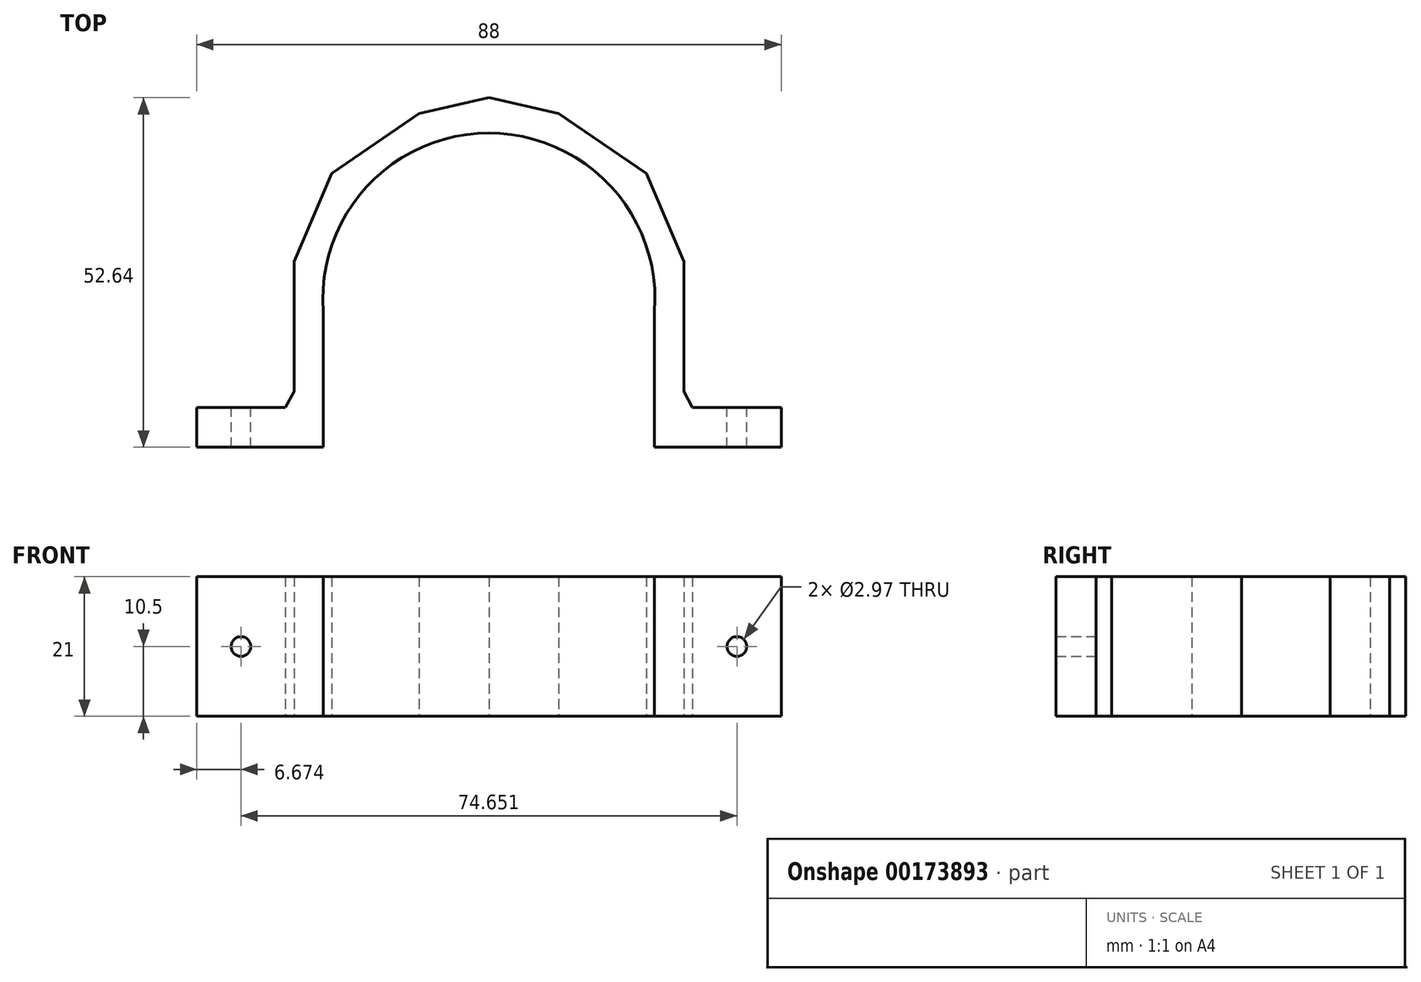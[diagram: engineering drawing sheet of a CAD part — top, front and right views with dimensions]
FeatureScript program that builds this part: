
annotation { "Feature Type Name" : "Feature", "Feature Type Description" : "" }
export const myFeature = defineFeature(function(context is Context, id is Id, definition is map)
    precondition{}
    {
        {
            var Q0;
            Q0=qCreatedBy(makeId("Top.planeOp"),FACE);
            var sketch = newSketch(context, id + "F0", { "sketchPlane" : qUnion([Q0])});
            skArc(sketch, "E0", {"start": v(24.93, 20.42) * mm, "mid": v(0, 47.3) * mm, "end": v(-24.93, 20.42) * mm});
            skLineSegment(sketch, "E1.bottom", {"start": v(28, 22.3) * mm, "end": v(-28, 22.3) * mm});
            skLineSegment(sketch, "E1.top", {"start": v(28, -22.3) * mm, "end": v(-28, -22.3) * mm});
            skPoint(sketch, "E1.middle", {"position": v(0, 0) * mm});
            skLineSegment(sketch, "E2", {"start": v(28, 0) * mm, "end": v(44, 0) * mm});
            skPoint(sketch, "E2.endSnap0", {"position": v(28, 0) * mm});
            skLineSegment(sketch, "E3", {"start": v(44, 0) * mm, "end": v(44, 6) * mm});
            skLineSegment(sketch, "E4", {"start": v(44, 6) * mm, "end": v(30.65, 6) * mm});
            skLineSegment(sketch, "E5", {"start": v(0, 54.2) * mm, "end": v(0, -14.37) * mm, "construction": true});
            skLineSegment(sketch, "E6.MirrorCS", {"start": v(-44, 6) * mm, "end": v(-30.65, 6) * mm});
            skLineSegment(sketch, "E7.MirrorCS", {"start": v(-44, 0) * mm, "end": v(-44, 6) * mm});
            skLineSegment(sketch, "E8.MirrorCS", {"start": v(-28, 0) * mm, "end": v(-44, 0) * mm});
            skLineSegment(sketch, "E9", {"start": v(-29.33, 8.4) * mm, "end": v(-30.65, 6) * mm});
            skLineSegment(sketch, "E10", {"start": v(-30.65, 6) * mm, "end": v(-29.33, 8.4) * mm});
            skLineSegment(sketch, "E11", {"start": v(-29.33, 8.4) * mm, "end": v(-29.33, 27.94) * mm});
            skLineSegment(sketch, "E12", {"start": v(-29.33, 27.94) * mm, "end": v(-23.7, 41.25) * mm});
            skLineSegment(sketch, "E13", {"start": v(-23.7, 41.25) * mm, "end": v(-10.51, 50.24) * mm});
            skLineSegment(sketch, "E14", {"start": v(-10.51, 50.24) * mm, "end": v(0, 52.64) * mm});
            skLineSegment(sketch, "E15.MirrorCS", {"start": v(10.51, 50.24) * mm, "end": v(0, 52.64) * mm});
            skLineSegment(sketch, "E16.MirrorCS", {"start": v(23.7, 41.25) * mm, "end": v(10.51, 50.24) * mm});
            skLineSegment(sketch, "E17.MirrorCS", {"start": v(29.33, 27.94) * mm, "end": v(23.7, 41.25) * mm});
            skLineSegment(sketch, "E18.MirrorCS", {"start": v(29.33, 8.4) * mm, "end": v(29.33, 27.94) * mm});
            skLineSegment(sketch, "E19.MirrorCS", {"start": v(30.65, 6) * mm, "end": v(29.33, 8.4) * mm});
            skPoint(sketch, "E20.orphan", {"position": v(-28, 6) * mm});
            skPoint(sketch, "E21.orphan", {"position": v(-28, 10.8) * mm});
            skPoint(sketch, "E22.orphan", {"position": v(28, 6) * mm});
            skLineSegment(sketch, "E23", {"start": v(-44, 0) * mm, "end": v(44, 0) * mm});
            skLineSegment(sketch, "E24", {"start": v(-24.93, 20.42) * mm, "end": v(-24.93, 0) * mm});
            skLineSegment(sketch, "E25.MirrorCS", {"start": v(24.93, 20.42) * mm, "end": v(24.93, 0) * mm});
            skSolve(sketch);
        }
        {
            var Q0;
            {var subQ7=sQuery(id+"F0.wireOp",EDGE,"E3");Q0=makeQuery(id+"F0.imprint","IMPRINT",FACE,{"disambiguationData":[TD([[makeQuery(id+"F0.imprint","IMPRINT",EDGE,{"derivedFrom":subQ7}),1.0]])]});}
            extrude(context, id + "F1", {"entities" : qUnion([Q0]), "depth" : 21 * mm});
        }
        {
            var Q0;
            Q0=makeQuery(id+"F1.opExtrude","SWEPT_FACE",FACE,{"disambiguationData":[OSD([sQuery(id+"F0.wireOp",EDGE,"E4")])]});
            var sketch = newSketch(context, id + "F2", { "sketchPlane" : qUnion([Q0])});
            skCircle(sketch, "E26", {"center": v(-37.33, 10.5) * mm, "radius": 1.48 * mm});
            skPoint(sketch, "E26.centerSnap0", {"position": v(-44, 10.5) * mm});
            skPoint(sketch, "E26.centerSnap1", {"position": v(-37.33, 21) * mm});
            skLineSegment(sketch, "E27", {"start": v(0, 25.83) * mm, "end": v(0, -3.1) * mm, "construction": true});
            skCircle(sketch, "E28.MirrorC", {"center": v(37.33, 10.5) * mm, "radius": 1.48 * mm});
            skSolve(sketch);
        }
        {
            var Q0;
            Q0 = qSketchRegion(id + "F2", true);
            extrude(context, id + "F3", {"entities" : qUnion([Q0]), "operationType" : NewBodyOperationType.REMOVE, "endBound" : BoundingType.THROUGH_ALL, "oppositeDirection" : true, "depth" : 25 * mm});
        }
    });
